# Revit family: rba-bim-b823
name_source: partatom
category: Specialty Equipment
revit_build: Autodesk Revit 2015 (Build: 20140223_1515(x64)
units: mm (PartAtom-declared; Revit-internal decimal feet)

## types (1)
- B-823
    ADA Compliant = Yes
    Assembly Code = C1030210
    Default Elevation = 0 mm  [stored 0 ft]
    Description = Bobrick Top-Fill Counter-Mounted Manual Foam Soap Dispenser
    Height = 133 mm
    Installation Type = Counter-Mounted
    Length = 102 mm
    Manufacturer = Bobrick Washroom Equipment, Inc
    Material = Stainless Steel-Bobrick-Polished
    Model = B-823
    Modified Issue = 20161117.01
    Specification = Top-fill counter-mounted manual foam soap dispenser shall dispense 7ml of foam using 0.5ml of commercially marketed foam soaps. Cover shall be constructed of durable die-cast zinc with bright polish finish. Spout assembly shall be type-304 stainless steel with bright polished finish. Dispenser shall be equipped with integrated funnel to facilitate re-filling of soap. Spout shall rotate 360° without damage to valve mechanism. Valve shall be operable with one hand and with less than 5 pounds of force (22.2 N) to comply with accessible design (including ADAAG in U.S.A.). Escutcheon shall lock to body with concealed locking mechanism that is opened with special key provided. Foam Dispensing assembly shall be removable from top for filling and maintenance. Shank shall accommodate mounting thicknesses up to 3'' (76mm). Translucent, shatter-resistant polyethylene container shall have a capacity of 34-fl oz (1.0-L).
    URL = http://www.rba.com.au
    Width = 65 mm

note: [stored X ft] marks values corroborated as IEEE doubles in the binary element streams (Revit-internal decimal feet)

## geometry (parser evidence)
native form markers: Sweep x2
no freeform markers — native parametric forms only
